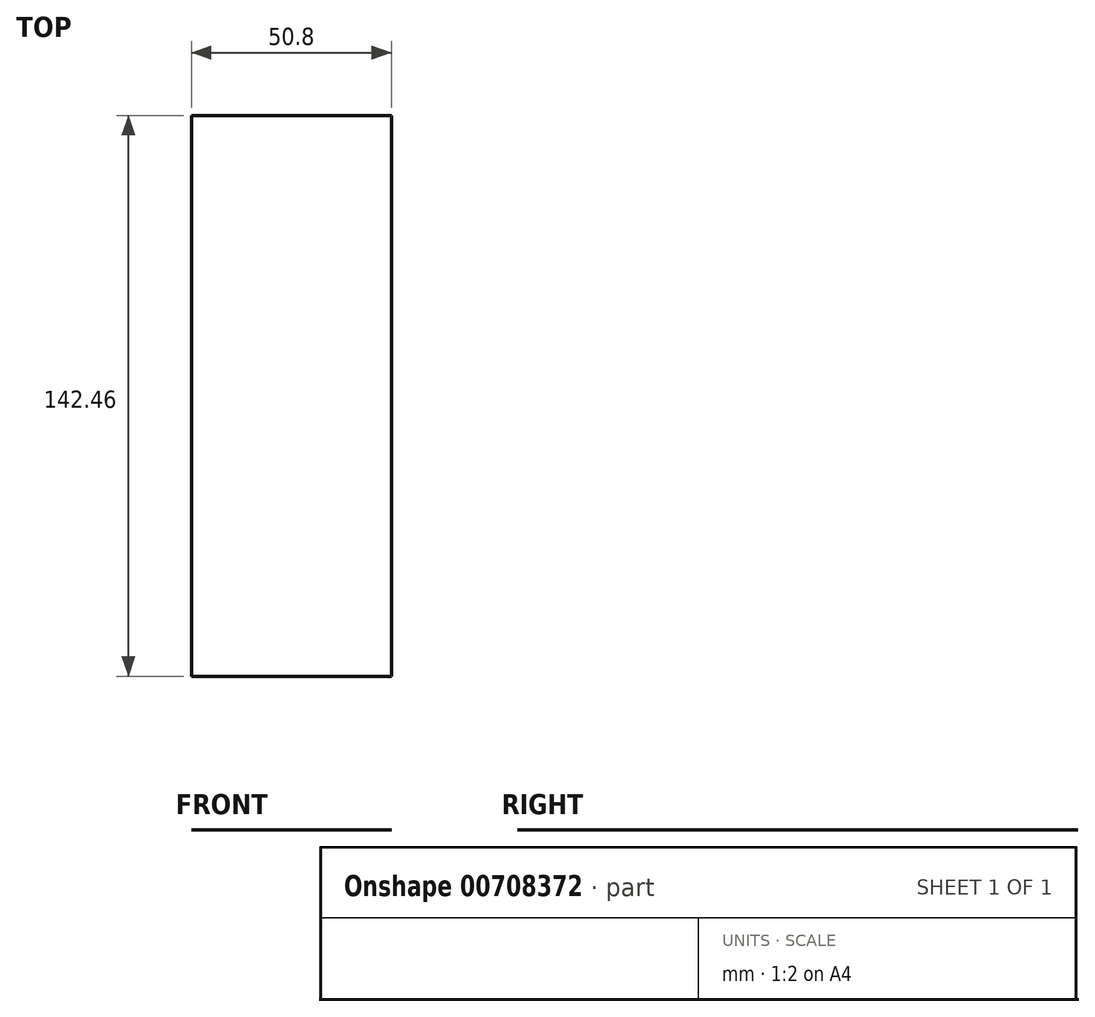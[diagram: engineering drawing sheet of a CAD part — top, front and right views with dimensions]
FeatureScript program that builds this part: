
annotation { "Feature Type Name" : "Feature", "Feature Type Description" : "" }
export const myFeature = defineFeature(function(context is Context, id is Id, definition is map)
    precondition{}
    {
        {
            var Q0;
            Q0=qCreatedBy(makeId("Right.planeOp"),FACE);
            var sketch = newSketch(context, id + "F0", { "sketchPlane" : qUnion([Q0])});
            skLineSegment(sketch, "E0", {"start": v(0, 0) * mm, "end": v(-142.46, 171.51) * mm});
            skLineSegment(sketch, "E1", {"start": v(-142.46, 171.51) * mm, "end": v(0, 171.51) * mm});
            skLineSegment(sketch, "E2", {"start": v(0, 171.51) * mm, "end": v(0, 0) * mm});
            skSolve(sketch);
        }
        {
            var Q0;
            Q0=makeQuery(id+"F0.imprint","IMPRINT",FACE,{"disambiguationData":[TD([[makeQuery(id+"F0.imprint","IMPRINT",EDGE,{"derivedFrom":sQuery(id+"F0.wireOp",EDGE,"E0")}),-1.0]])]});
            var sketch = newSketch(context, id + "F1", { "sketchPlane" : qUnion([Q0])});
            skSolve(sketch);
        }
        {
            var Q0;
            Q0=makeQuery(id+"F1.imprint","IMPRINT",FACE,{"disambiguationData":[TD([[makeQuery(id+"F1.imprint","IMPRINT",EDGE,{"derivedFrom":makeQuery(id+"F0.imprint","IMPRINT",EDGE,{"derivedFrom":sQuery(id+"F0.wireOp",EDGE,"E0")})}),-1.0]])]});
            var sketch = newSketch(context, id + "F2", { "sketchPlane" : qUnion([Q0])});
            skSolve(sketch);
        }
        {
            var Q0;
            Q0 = qSketchRegion(id + "F2", true);
            var Q1;
            Q1=sQuery(id+"F0.wireOp",EDGE,"E1");
            extrude(context, id + "F3", {"entities" : qUnion([Q0]), "bodyType" : ToolBodyType.SURFACE, "operationType" : NewBodyOperationType.ADD, "surfaceEntities" : qUnion([Q1]), "oppositeDirection" : true, "depth" : 25.4 * mm, "hasOffset" : true, "offsetDistance" : 76.2 * mm, "hasDraft" : true, "draftAngle" : 3 * degree, "hasSecondDirection" : true, "secondDirectionOppositeDirection" : false, "secondDirectionDepth" : 25.4 * mm});
        }
    });
